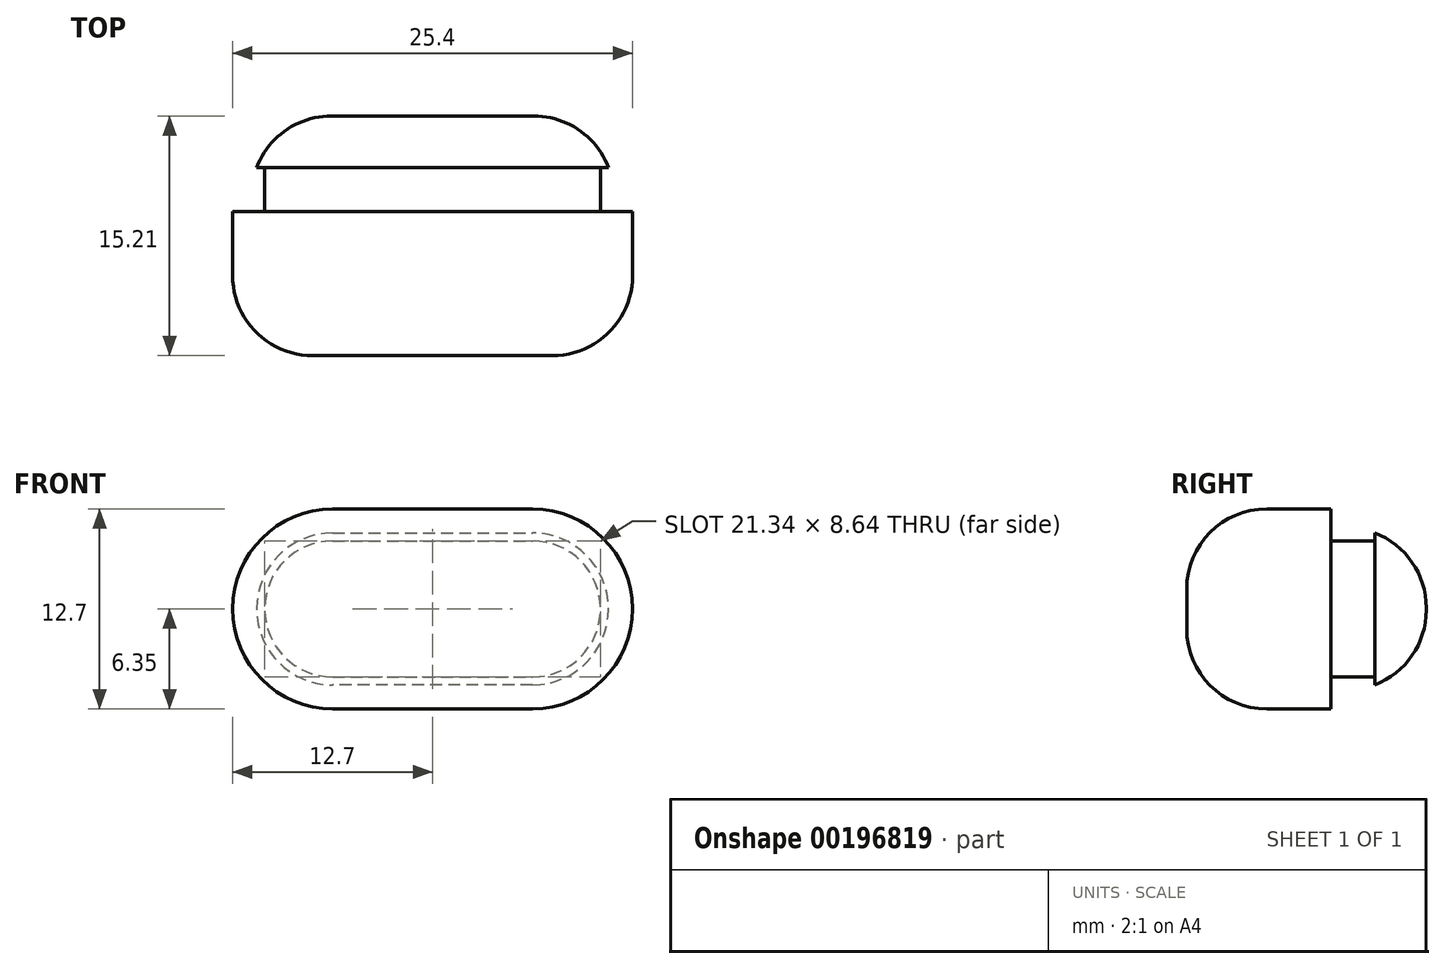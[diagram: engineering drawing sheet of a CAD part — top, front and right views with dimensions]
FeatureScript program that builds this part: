
annotation { "Feature Type Name" : "Feature", "Feature Type Description" : "" }
export const myFeature = defineFeature(function(context is Context, id is Id, definition is map)
    precondition{}
    {
        {
            var Q0;
            Q0=qCreatedBy(makeId("Front.planeOp"),FACE);
            var sketch = newSketch(context, id + "F0", { "sketchPlane" : qUnion([Q0])});
            skLineSegment(sketch, "E0.bottom", {"start": v(0, 12.7) * mm, "end": v(12.7, 12.7) * mm});
            skLineSegment(sketch, "E0.top", {"start": v(0, 0) * mm, "end": v(12.7, 0) * mm});
            skArc(sketch, "E1", {"start": v(0, 12.7) * mm, "mid": v(-6.35, 6.35) * mm, "end": v(0, 0) * mm});
            skArc(sketch, "E2", {"start": v(12.7, 0) * mm, "mid": v(19.05, 6.35) * mm, "end": v(12.7, 12.7) * mm});
            skSolve(sketch);
        }
        {
            var Q0;
            Q0 = qSketchRegion(id + "F0", true);
            extrude(context, id + "F1", {"entities" : qUnion([Q0]), "depth" : 9.14 * mm});
        }
        {
            var Q0;
            Q0=makeQuery(id+"F1.opExtrude","CAP_FACE",FACE,{"disambiguationData":[OSD([sQuery(id+"F0.wireOp",EDGE,"E0.bottom"),sQuery(id+"F0.wireOp",EDGE,"E0.top"),sQuery(id+"F0.wireOp",EDGE,"E1"),sQuery(id+"F0.wireOp",EDGE,"E2")])],"isStart":true});
            var sketch = newSketch(context, id + "F2", { "sketchPlane" : qUnion([Q0])});
            skLineSegment(sketch, "E3.0", {"start": v(0, 10.67) * mm, "end": v(-12.7, 10.67) * mm});
            skArc(sketch, "E3.1", {"start": v(0, 10.67) * mm, "mid": v(4.32, 6.35) * mm, "end": v(0, 2.03) * mm});
            skLineSegment(sketch, "E3.2", {"start": v(0, 2.03) * mm, "end": v(-12.7, 2.03) * mm});
            skArc(sketch, "E3.3", {"start": v(-12.7, 2.03) * mm, "mid": v(-17.02, 6.35) * mm, "end": v(-12.7, 10.67) * mm});
            skSolve(sketch);
        }
        {
            var Q0;
            Q0=makeQuery(id+"F2.imprint","IMPRINT",FACE,{"disambiguationData":[TD([[makeQuery(id+"F2.imprint","IMPRINT",EDGE,{"derivedFrom":sQuery(id+"F2.wireOp",EDGE,"E3.0")}),1.0]])]});
            extrude(context, id + "F3", {"entities" : qUnion([Q0]), "operationType" : NewBodyOperationType.ADD, "depth" : 2.8 * mm});
        }
        {
            var Q0;
            Q0=makeQuery(id+"F3.opExtrude","CAP_FACE",FACE,{"disambiguationData":[OSD([sQuery(id+"F2.wireOp",EDGE,"E3.0"),sQuery(id+"F2.wireOp",EDGE,"E3.1"),sQuery(id+"F2.wireOp",EDGE,"E3.2"),sQuery(id+"F2.wireOp",EDGE,"E3.3")])],"isStart":false});
            var sketch = newSketch(context, id + "F4", { "sketchPlane" : qUnion([Q0])});
            skArc(sketch, "E4.0", {"start": v(0, 1.52) * mm, "mid": v(4.83, 6.35) * mm, "end": v(0, 11.18) * mm});
            skLineSegment(sketch, "E4.1", {"start": v(-12.7, 1.52) * mm, "end": v(0, 1.52) * mm});
            skArc(sketch, "E4.2", {"start": v(-12.7, 11.18) * mm, "mid": v(-17.53, 6.35) * mm, "end": v(-12.7, 1.52) * mm});
            skLineSegment(sketch, "E4.3", {"start": v(0, 11.18) * mm, "end": v(-12.7, 11.18) * mm});
            skSolve(sketch);
        }
        {
            var Q0;
            Q0 = qSketchRegion(id + "F4", true);
            extrude(context, id + "F5", {"entities" : qUnion([Q0]), "operationType" : NewBodyOperationType.ADD, "depth" : 3.28 * mm});
        }
        {
            var Q0;
            Q0=makeQuery(id+"F5.opExtrude","CAP_EDGE",EDGE,{"disambiguationData":[OSD([sQuery(id+"F4.wireOp",EDGE,"E4.2")])],"isStart":false});
            var Q1;
            Q1=makeQuery(id+"F5.opExtrude","CAP_EDGE",EDGE,{"disambiguationData":[OSD([sQuery(id+"F4.wireOp",EDGE,"E4.3")])],"isStart":false});
            var Q2;
            Q2=makeQuery(id+"F5.opExtrude","CAP_EDGE",EDGE,{"disambiguationData":[OSD([sQuery(id+"F4.wireOp",EDGE,"E4.0")])],"isStart":false});
            var Q3;
            Q3=makeQuery(id+"F5.opExtrude","CAP_EDGE",EDGE,{"disambiguationData":[OSD([sQuery(id+"F4.wireOp",EDGE,"E4.1")])],"isStart":false});
            fillet(context, id + "F6", {"entities" : qUnion([Q0, Q1, Q2, Q3]), "radius" : 5.08 * mm, "tangentPropagation" : true, "allowEdgeOverflow" : false});
        }
        {
            var Q0;
            Q0=makeQuery(id+"F1.opExtrude","CAP_EDGE",EDGE,{"disambiguationData":[OSD([sQuery(id+"F0.wireOp",EDGE,"E0.bottom")])],"isStart":false});
            var Q1;
            Q1=makeQuery(id+"F1.opExtrude","CAP_EDGE",EDGE,{"disambiguationData":[OSD([sQuery(id+"F0.wireOp",EDGE,"E2")])],"isStart":false});
            var Q2;
            Q2=makeQuery(id+"F1.opExtrude","CAP_EDGE",EDGE,{"disambiguationData":[OSD([sQuery(id+"F0.wireOp",EDGE,"E0.top")])],"isStart":false});
            var Q3;
            Q3=makeQuery(id+"F1.opExtrude","CAP_EDGE",EDGE,{"disambiguationData":[OSD([sQuery(id+"F0.wireOp",EDGE,"E1")])],"isStart":false});
            fillet(context, id + "F7", {"entities" : qUnion([Q0, Q1, Q2, Q3]), "radius" : 5.08 * mm, "tangentPropagation" : true, "allowEdgeOverflow" : false});
        }
    });
